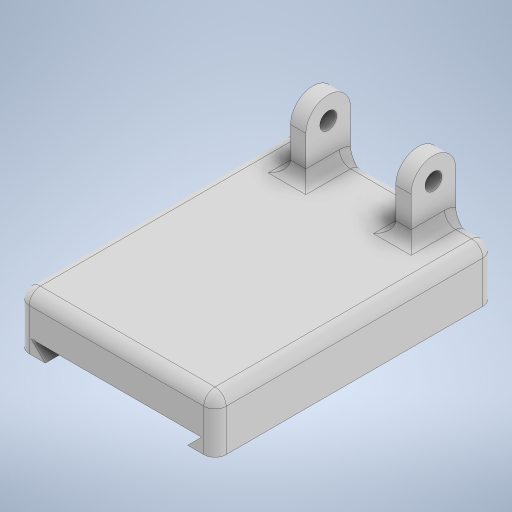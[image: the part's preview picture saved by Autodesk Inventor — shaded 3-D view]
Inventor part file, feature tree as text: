
AUTODESK INVENTOR PART (.ipt)
format: ipt  version: 2024 (Build 280153000, 153)  size: 397,824 bytes
history: native  units: mm
features: extrude x7, sketch x7, fillet x4, mirror x2, other x1
ambient origin geometry x8: Origin, YZ Plane, XZ Plane, XY Plane, X Axis, Y Axis, Z Axis, Center Point
bodies: Body1 (feature_tree)
feature tree (21):
  other  "Bryła1"
  extrude  "Wyciągnięcie proste1"  Depth=70.6mm
  extrude  "Wyciągnięcie proste2"  Depth=100.0mm
  fillet  "Zaokrąglenie1"  Radius=55.0mm
  extrude  "Wyciągnięcie proste3"  Depth=35.3mm
  mirror  "Odbij1"
  extrude  "Wyciągnięcie proste4"  Depth=19.0mm TaperAngle=0.0deg
  fillet  "Zaokrąglenie2"  [1 undecoded]
  fillet  "Zaokrąglenie3"  [1 undecoded]
  extrude  "Wyciągnięcie proste5"  Depth=5.0mm
  extrude  "Wyciągnięcie proste8"  Depth=30.5mm
  fillet  "Zaokrąglenie4"  Radius=61.0mm
  extrude  "Wyciągnięcie proste9"  Depth=80.3mm TaperAngle=0.0deg
  mirror  "Odbij2"
  sketch  "Szkic3"
  sketch  "Szkic4"
  sketch  "Szkic5"
  sketch  "Szkic6"
  sketch  "Szkic7"
  sketch  "Szkic8"
  sketch  "Szkic9"
note: 2 required parameter values undecoded (feature->parameter linkage not recoverable at this tier; creation-order binding heuristic only, values carry confidence <= 0.55)
